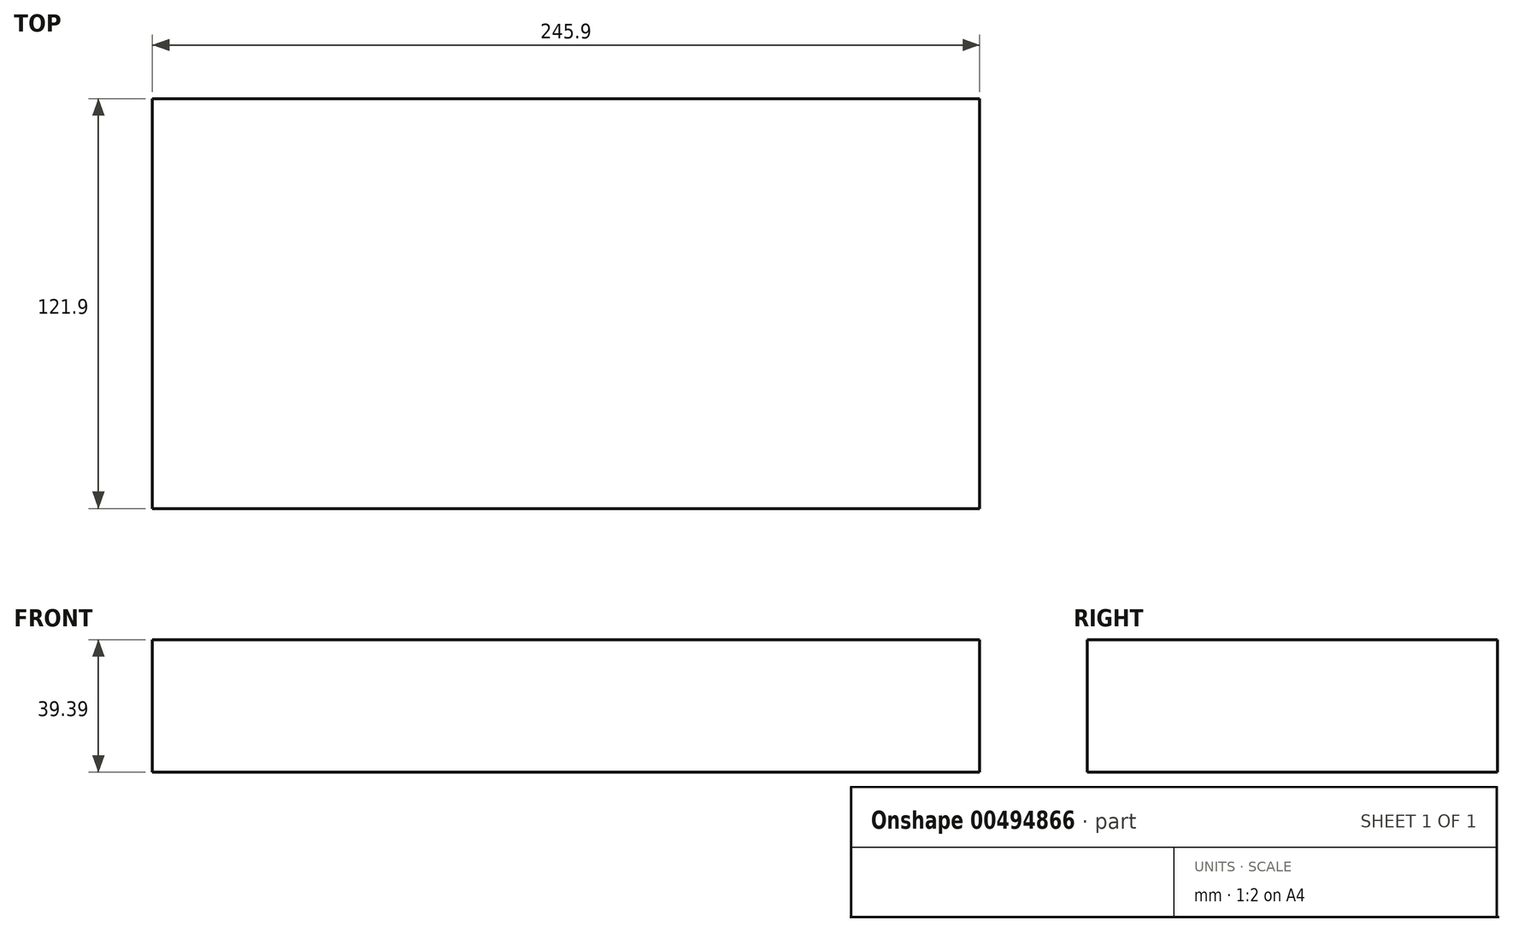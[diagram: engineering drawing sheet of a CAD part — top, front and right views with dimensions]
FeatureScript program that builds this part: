
annotation { "Feature Type Name" : "Feature", "Feature Type Description" : "" }
export const myFeature = defineFeature(function(context is Context, id is Id, definition is map)
    precondition{}
    {
        {
            var Q0;
            Q0=qCreatedBy(makeId("Right.planeOp"),FACE);
            var sketch = newSketch(context, id + "F0", { "sketchPlane" : qUnion([Q0])});
            skLineSegment(sketch, "E0.bottom", {"start": v(60.95, 21.6) * mm, "end": v(-60.95, 21.6) * mm});
            skLineSegment(sketch, "E0.top", {"start": v(60.95, 61) * mm, "end": v(-60.95, 61) * mm});
            skLineSegment(sketch, "E0.left", {"start": v(60.95, 21.6) * mm, "end": v(60.95, 61) * mm});
            skLineSegment(sketch, "E0.right", {"start": v(-60.95, 21.6) * mm, "end": v(-60.95, 61) * mm});
            skPoint(sketch, "E0.middle", {"position": v(0, 41.3) * mm});
            skSolve(sketch);
        }
        {
            var Q0;
            Q0 = qSketchRegion(id + "F0", true);
            extrude(context, id + "F1", {"entities" : qUnion([Q0]), "depth" : 125.9 * mm});
        }
        {
            var Q0;
            Q0=makeQuery(id+"F1.opExtrude","CAP_FACE",FACE,{"disambiguationData":[OSD([sQuery(id+"F0.wireOp",EDGE,"E0.bottom"),sQuery(id+"F0.wireOp",EDGE,"E0.top"),sQuery(id+"F0.wireOp",EDGE,"E0.left"),sQuery(id+"F0.wireOp",EDGE,"E0.right")])],"isStart":false});
            extrude(context, id + "F2", {"entities" : qUnion([Q0]), "operationType" : NewBodyOperationType.ADD, "depth" : 120 * mm});
        }
    });
